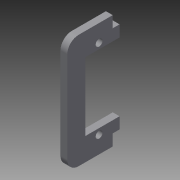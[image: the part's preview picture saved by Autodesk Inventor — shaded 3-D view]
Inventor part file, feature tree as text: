
AUTODESK INVENTOR PART (.ipt)
format: ipt  version: 2013 (Build 170138000, 138)  size: 106,496 bytes
history: native  units: in
note: dims shown in document units (in); Inventor stores cm internally (conversion verified against a paired STEP export)
features: extrude x2, sketch x2
ambient origin geometry x8: Origin, YZ Plane, XZ Plane, XY Plane, X Axis, Y Axis, Z Axis, Center Point
bodies: Solid1 (feature_tree)
feature tree (4):
  extrude  "Extrusion1"  Depth=0.1181in
  extrude  "Extrusion2"  Depth=0.7874in
  sketch  "Sketch1"  dims[d0=0.1969in d1=0.1181in]
  sketch  "Sketch3"  dims[d2=0.1969in d3=0.7874in d4=1.1811in d5=0.4724in d6=0.1969in d7=0.1181in d8=0.1969in d9=0.1969in d10=0.1181in d11=0.0in d12=0.1181in d14=0.1181in d15=0.2362in d16=0.2362in d17=0.0984in d18=0.0984in d19=0.1181in d20=0.0in]
